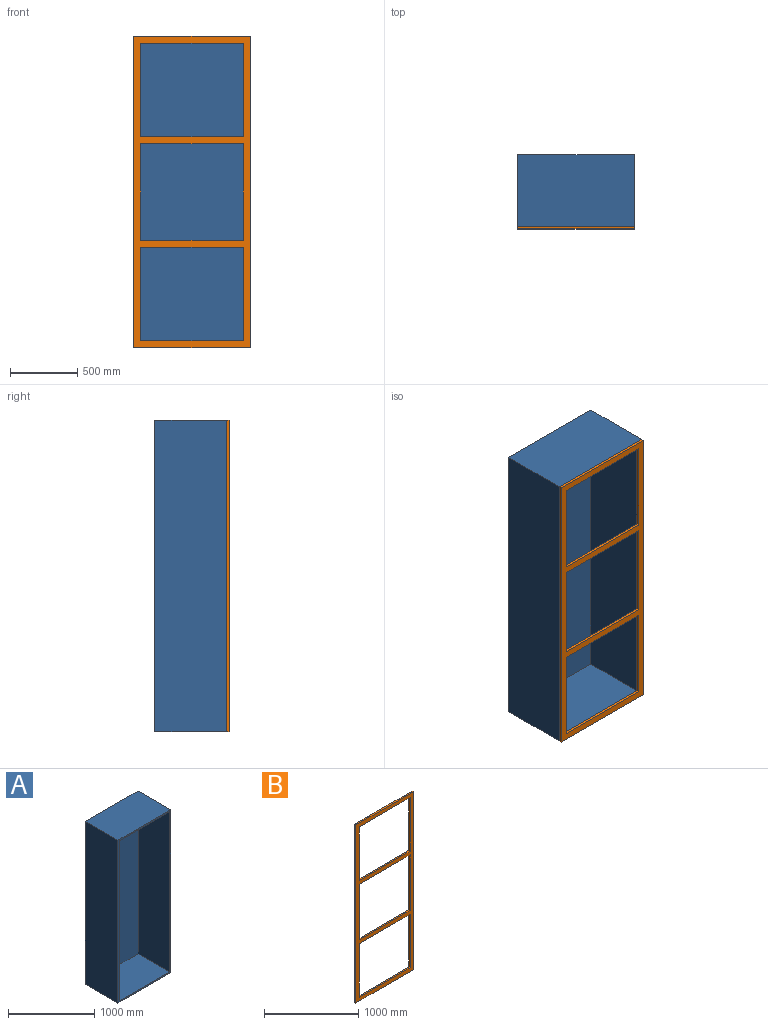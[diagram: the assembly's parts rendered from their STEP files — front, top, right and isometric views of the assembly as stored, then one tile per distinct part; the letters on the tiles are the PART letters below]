
ASSEMBLY  parts=2 mates=1
PART A: 11 faces, bbox 863.6x533.4x2311.4 mm
  f0: plane 2311.4x863.6mm, normal (0,1,0), area 1996125mm2, adj f1,f2,f3,f4
  f1: plane 2311.4x533.4mm, normal (-1,0,0), area 1232900.8mm2, adj f0,f2,f4,f5
  f2: plane 863.6x533.4mm, normal (0,0,-1), area 460644.2mm2, adj f0,f1,f3,f5
  f3: plane 2311.4x533.4mm, normal (1,0,0), area 1232900.8mm2, adj f0,f2,f4,f5
  f4: plane 863.6x533.4mm, normal (0,0,1), area 460644.2mm2, adj f0,f1,f3,f5
  f5: plane 2311.4x863.6mm, normal (0,-1,0), area 119515.9mm2, adj f1,f2,f3,f4,f7,f8,f9,f10
  f6: plane 2273.3x825.5mm, normal (0,-1,0), area 1876609.1mm2, adj f7,f8,f9,f10
  f7: plane 825.5x514.35mm, normal (0,0,1), area 424595.9mm2, adj f5,f6,f8,f9
  f8: plane 2273.3x514.35mm, normal (1,0,0), area 1169271.9mm2, adj f5,f6,f7,f10
  f9: plane 2273.3x514.35mm, normal (-1,0,0), area 1169271.9mm2, adj f5,f6,f7,f10
  f10: plane 825.5x514.35mm, normal (0,0,-1), area 424595.9mm2, adj f5,f6,f8,f9
PART B: 18 faces, bbox 863.6x19.1x2311.4 mm
  f0: plane 694.27x19.05mm, normal (-1,0,0), area 13225.8mm2, adj f1,f15,f16,f17
  f1: plane 762x19.05mm, normal (0,0,1), area 14516.1mm2, adj f0,f2,f16,f17
  f2: plane 694.27x19.05mm, normal (1,0,0), area 13225.8mm2, adj f1,f15,f16,f17
  f3: plane 762x19.05mm, normal (0,0,-1), area 14516.1mm2, adj f4,f12,f16,f17
  f4: plane 719.67x19.05mm, normal (-1,0,0), area 13709.7mm2, adj f3,f5,f16,f17
  f5: plane 762x19.05mm, normal (0,0,1), area 14516.1mm2, adj f4,f12,f16,f17
  f6: plane 762x19.05mm, normal (0,0,1), area 14516.1mm2, adj f7,f13,f16,f17
  f7: plane 694.27x19.05mm, normal (1,0,0), area 13225.8mm2, adj f6,f8,f16,f17
  f8: plane 762x19.05mm, normal (0,0,-1), area 14516.1mm2, adj f7,f13,f16,f17
  f9: plane 2311.4x19.05mm, normal (-1,0,0), area 44032.2mm2, adj f10,f14,f16,f17
  f10: plane 863.6x19.05mm, normal (0,0,-1), area 16451.6mm2, adj f9,f11,f16,f17
  f11: plane 2311.4x19.05mm, normal (1,0,0), area 44032.2mm2, adj f10,f14,f16,f17
  f12: plane 719.67x19.05mm, normal (1,0,0), area 13709.7mm2, adj f3,f5,f16,f17
  f13: plane 694.27x19.05mm, normal (-1,0,0), area 13225.8mm2, adj f6,f8,f16,f17
  f14: plane 863.6x19.05mm, normal (0,0,1), area 16451.6mm2, adj f9,f11,f16,f17
  f15: plane 762x19.05mm, normal (0,0,-1), area 14516.1mm2, adj f0,f2,f16,f17
  f16: plane 2311.4x863.6mm, normal (0,1,0), area 389676.6mm2, adj f0,f1,f2,f3,f4,f5,f6,f7
  f17: plane 2311.4x863.6mm, normal (0,-1,0), area 389676.6mm2, adj f0,f1,f2,f3,f4,f5,f6,f7
PLACE A t=(-573.47,-99.01,1175.46)mm
PLACE B t=(-573.47,-118.06,1560.69)mm
MATE fastened A.f5 <-> B.f16  axis (0,-1,0) through (-573.47,-99.01,1175.46)mm
